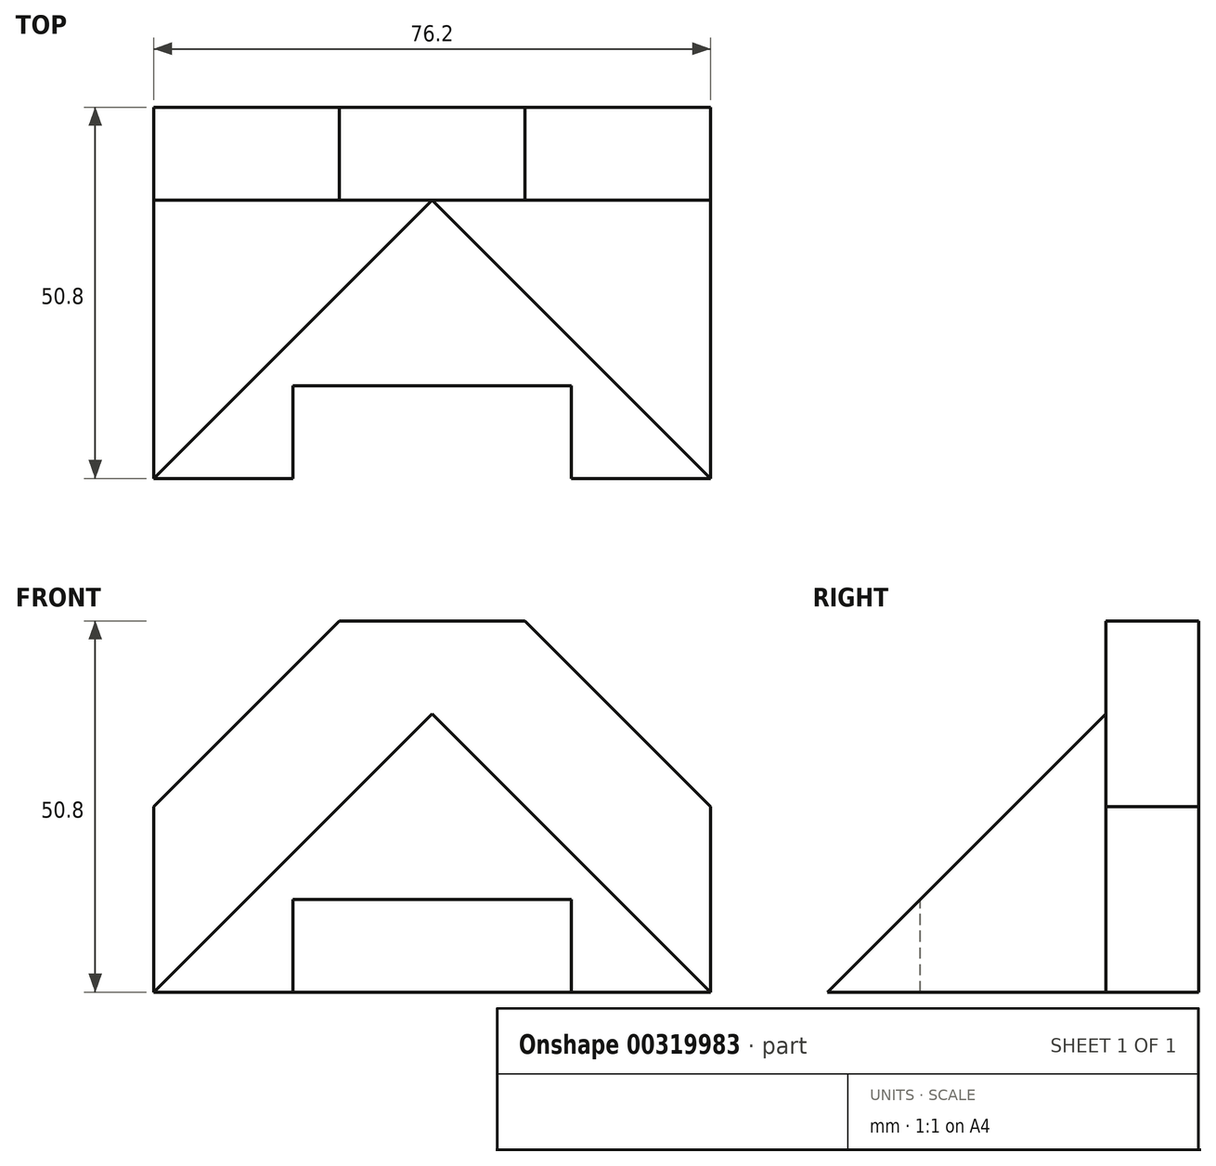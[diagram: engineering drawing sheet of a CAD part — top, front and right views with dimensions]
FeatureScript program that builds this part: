
annotation { "Feature Type Name" : "Feature", "Feature Type Description" : "" }
export const myFeature = defineFeature(function(context is Context, id is Id, definition is map)
    precondition{}
    {
        {
            var Q0;
            Q0=qCreatedBy(makeId("Front.planeOp"),FACE);
            var sketch = newSketch(context, id + "F0", { "sketchPlane" : qUnion([Q0])});
            skLineSegment(sketch, "E0", {"start": v(0, 0) * mm, "end": v(0, 25.4) * mm});
            skLineSegment(sketch, "E1", {"start": v(0, 25.4) * mm, "end": v(25.4, 50.8) * mm});
            skLineSegment(sketch, "E2", {"start": v(25.4, 50.8) * mm, "end": v(50.8, 50.8) * mm});
            skLineSegment(sketch, "E3", {"start": v(50.8, 50.8) * mm, "end": v(76.2, 25.4) * mm});
            skLineSegment(sketch, "E4", {"start": v(76.2, 25.4) * mm, "end": v(76.2, 0) * mm});
            skLineSegment(sketch, "E5", {"start": v(76.2, 0) * mm, "end": v(0, 0) * mm});
            skSolve(sketch);
        }
        {
            var Q0;
            Q0 = qSketchRegion(id + "F0", true);
            extrude(context, id + "F1", {"entities" : qUnion([Q0]), "depth" : 12.7 * mm});
        }
        {
            var Q0;
            Q0=makeQuery(id+"F1.opExtrude","CAP_FACE",FACE,{"disambiguationData":[OSD([sQuery(id+"F0.wireOp",EDGE,"E0"),sQuery(id+"F0.wireOp",EDGE,"E1"),sQuery(id+"F0.wireOp",EDGE,"E2"),sQuery(id+"F0.wireOp",EDGE,"E3"),sQuery(id+"F0.wireOp",EDGE,"E4"),sQuery(id+"F0.wireOp",EDGE,"E5")])],"isStart":false});
            var sketch = newSketch(context, id + "F2", { "sketchPlane" : qUnion([Q0])});
            skLineSegment(sketch, "E6", {"start": v(0, 0) * mm, "end": v(38.1, 38.1) * mm});
            skLineSegment(sketch, "E7", {"start": v(38.1, 38.1) * mm, "end": v(76.2, 0) * mm});
            skLineSegment(sketch, "E8", {"start": v(76.2, 0) * mm, "end": v(0, 0) * mm});
            skSolve(sketch);
        }
        {
            var Q0;
            Q0 = qSketchRegion(id + "F2", true);
            extrude(context, id + "F3", {"entities" : qUnion([Q0]), "operationType" : NewBodyOperationType.ADD, "depth" : 38.1 * mm});
        }
        {
            var Q0;
            Q0=makeQuery(id+"F1.opExtrude","SWEPT_FACE",FACE,{"disambiguationData":[OSD([sQuery(id+"F0.wireOp",EDGE,"E4")])]});
            var sketch = newSketch(context, id + "F4", { "sketchPlane" : qUnion([Q0])});
            skLineSegment(sketch, "E9.0.0", {"start": v(-12.7, 0) * mm, "end": v(-12.7, 38.1) * mm});
            skLineSegment(sketch, "E9.0.1", {"start": v(-12.7, 38.1) * mm, "end": v(-50.8, 38.1) * mm});
            skLineSegment(sketch, "E9.0.2", {"start": v(-50.8, 38.1) * mm, "end": v(-50.8, 0) * mm});
            skLineSegment(sketch, "E9.0.3", {"start": v(-50.8, 0) * mm, "end": v(-12.7, 0) * mm});
            skLineSegment(sketch, "E10", {"start": v(-12.7, 38.1) * mm, "end": v(-50.8, 0) * mm});
            skLineSegment(sketch, "E11", {"start": v(-50.8, 38.1) * mm, "end": v(-12.7, 38.1) * mm});
            skSolve(sketch);
        }
        {
            var Q0;
            Q0=makeQuery(id+"F4.imprint","IMPRINT",FACE,{"disambiguationData":[TD([[makeQuery(id+"F4.imprint","IMPRINT",EDGE,{"derivedFrom":sQuery(id+"F4.wireOp",EDGE,"E9.0.2")}),1.0]])]});
            extrude(context, id + "F5", {"entities" : qUnion([Q0]), "operationType" : NewBodyOperationType.REMOVE, "oppositeDirection" : true, "depth" : 76.2 * mm});
        }
        {
            var Q0;
            Q0=qCreatedBy(makeId("Front.planeOp"),FACE);
            cPlane(context, id + "F6", {"entities" : qUnion([Q0]), "cplaneType" : CPlaneType.OFFSET, "offset" : 50.8 * mm, "width" : 152.4 * mm, "height" : 152.4 * mm});
        }
        {
            var Q0;
            Q0=qCreatedBy(id+"F6.planeOp",FACE);
            var sketch = newSketch(context, id + "F7", { "sketchPlane" : qUnion([Q0])});
            skLineSegment(sketch, "E12.0.0", {"start": v(38.1, 38.1) * mm, "end": v(0, 0) * mm});
            skLineSegment(sketch, "E12.0.1", {"start": v(0, 0) * mm, "end": v(76.2, 0) * mm});
            skLineSegment(sketch, "E12.0.2", {"start": v(76.2, 0) * mm, "end": v(38.1, 38.1) * mm});
            skLineSegment(sketch, "E13", {"start": v(19.05, 0) * mm, "end": v(19.05, 12.7) * mm});
            skLineSegment(sketch, "E14", {"start": v(19.05, 12.7) * mm, "end": v(57.15, 12.7) * mm});
            skLineSegment(sketch, "E15", {"start": v(57.15, 12.7) * mm, "end": v(57.15, 0) * mm});
            skLineSegment(sketch, "E16", {"start": v(57.15, 0) * mm, "end": v(19.05, 0) * mm});
            skSolve(sketch);
        }
        {
            var Q0;
            Q0=makeQuery(id+"F7.imprint","IMPRINT",FACE,{"disambiguationData":[TD([[makeQuery(id+"F7.imprint","IMPRINT",EDGE,{"derivedFrom":sQuery(id+"F7.wireOp",EDGE,"E13")}),-1.0]])]});
            extrude(context, id + "F8", {"entities" : qUnion([Q0]), "operationType" : NewBodyOperationType.REMOVE, "oppositeDirection" : true, "depth" : 12.7 * mm});
        }
    });
